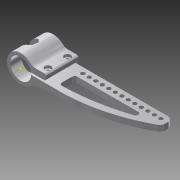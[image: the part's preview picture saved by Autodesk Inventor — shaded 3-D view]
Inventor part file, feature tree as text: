
AUTODESK INVENTOR PART (.ipt)
format: ipt  version: 2015 (Build 190159000, 159)  size: 228,352 bytes
history: native  units: mm
features: sketch x5, fillet x4, extrude x3, hole x2
ambient origin geometry x8: Origin, YZ Plane, XZ Plane, XY Plane, X Axis, Y Axis, Z Axis, Center Point
bodies: Solid1 (feature_tree)
feature tree (14):
  extrude  "Extrusion1"  Depth=42.0mm
  hole  "Hole1"  [1 undecoded]
  hole  "Hole2"  [1 undecoded]
  sketch  "Sketch3"  dims[d2=168.0mm d3=9.0mm]
  fillet  "Fillet1"  Radius=39.0mm
  sketch  "Sketch4"  dims[d4=50.0mm d7=3.0mm d8=39.0mm]
  extrude  "Extrusion3"  Depth=3.0mm
  extrude  "Extrusion4"  Depth=10.0mm
  fillet  "Fillet2"  Radius=50.0mm
  fillet  "Fillet3"  Radius=2.5mm
  fillet  "Fillet4"  Radius=17.0mm
  sketch  "Sketch1"  dims[d0=32.0mm d1=42.0mm]
  sketch  "Sketch5"  dims[d9=9.0mm d10=3.0mm]
  sketch  "Sketch8"  dims[d11=39.0mm d12=10.0mm d13=50.0mm d14=0.0mm d15=10.0mm d16=7.0mm d17=5.5mm d18=6.0mm d19=10.0mm d20=4.0mm d21=90.0deg d22=8.0mm d23=20.594885mm d24=10.0mm d25=7.0mm d26=5.5mm d27=6.0mm d28=10.0mm d29=4.0mm d30=90.0deg d31=8.0mm d32=20.594885mm d40=2.5mm d41=17.0mm d42=40.0mm d43=16.0mm d44=40.0mm d45=8.0mm d46=10.0mm d47=0.0mm d49=50.0mm d50=17.0mm d54=4.0mm d55=8.5mm d56=6.2mm d57=130.0mm d59=10.0mm d60=10.0mm d62=10.0mm d66=130.0mm d68=10.0mm d69=10.0mm d70=0.0mm d71=4.0mm d72=4.0mm d73=120.0mm d74=23.975256mm d75=8.0mm]
note: 2 required parameter values undecoded (feature->parameter linkage not recoverable at this tier; creation-order binding heuristic only, values carry confidence <= 0.55)
